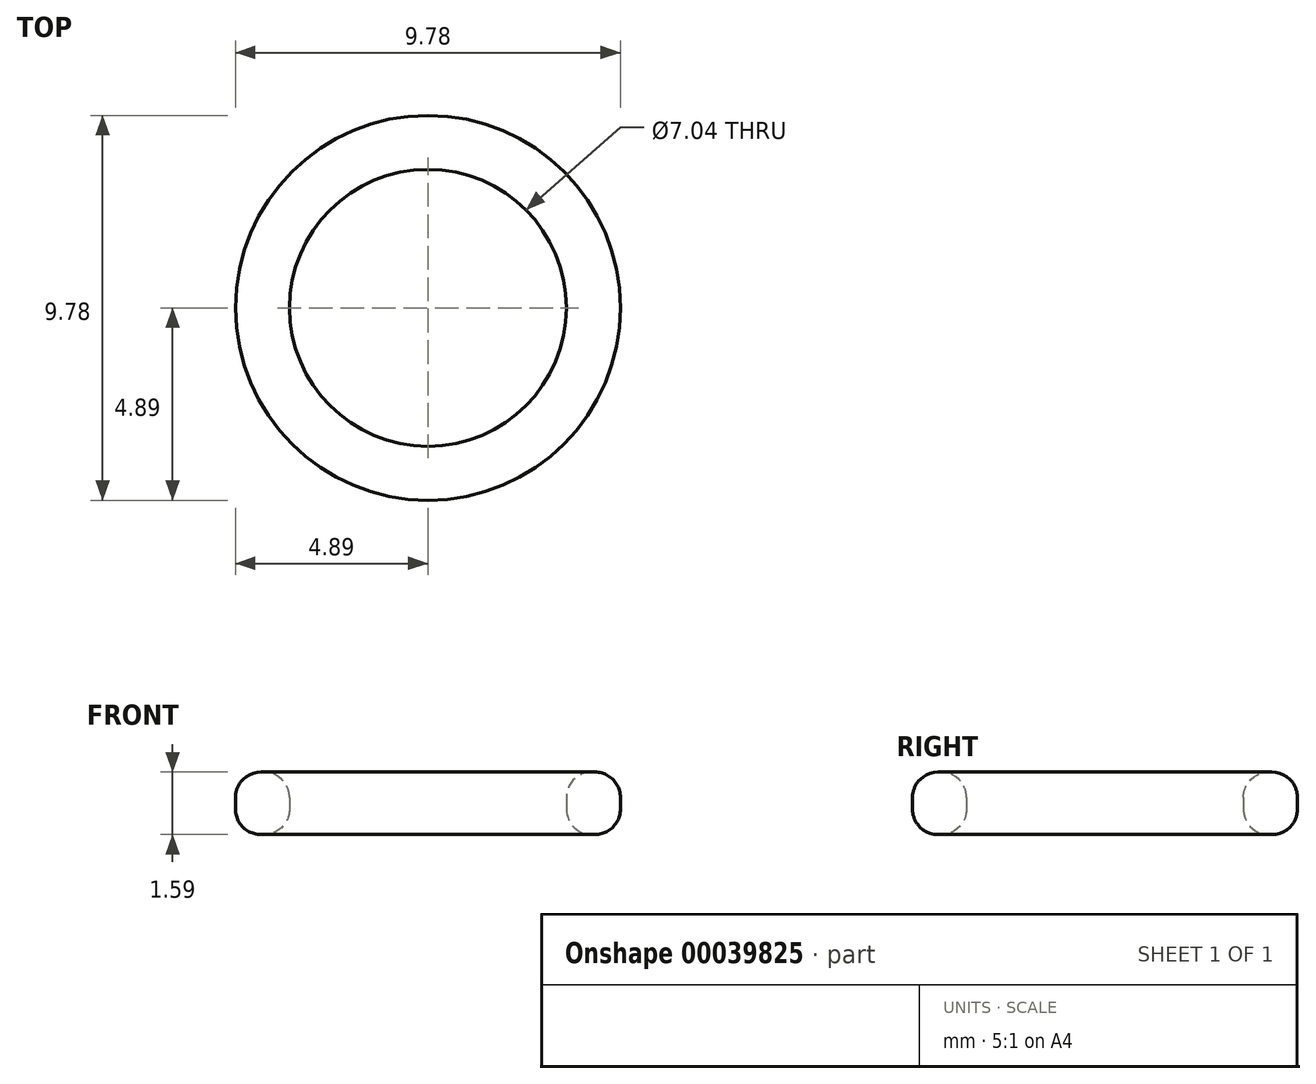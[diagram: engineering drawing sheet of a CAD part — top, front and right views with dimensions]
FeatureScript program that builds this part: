
annotation { "Feature Type Name" : "Feature", "Feature Type Description" : "" }
export const myFeature = defineFeature(function(context is Context, id is Id, definition is map)
    precondition{}
    {
        {
            var Q0;
            Q0=qCreatedBy(makeId("Top.planeOp"),FACE);
            var sketch = newSketch(context, id + "F0", { "sketchPlane" : qUnion([Q0])});
            skCircle(sketch, "E0", {"center": v(0, 0) * mm, "radius": 3.52 * mm});
            skCircle(sketch, "E1", {"center": v(0, 0) * mm, "radius": 4.89 * mm});
            skSolve(sketch);
        }
        {
            var Q0;
            Q0 = qSketchRegion(id + "F0", true);
            extrude(context, id + "F1", {"entities" : qUnion([Q0]), "depth" : 1.59 * mm});
        }
        {
            var Q0;
            Q0=makeQuery(id+"F1.opExtrude","CAP_EDGE",EDGE,{"disambiguationData":[OSD([sQuery(id+"F0.wireOp",EDGE,"E0")])],"isStart":false});
            var Q1;
            Q1=makeQuery(id+"F1.opExtrude","CAP_EDGE",EDGE,{"disambiguationData":[OSD([sQuery(id+"F0.wireOp",EDGE,"E1")])],"isStart":false});
            var Q2;
            Q2=makeQuery(id+"F1.opExtrude","CAP_EDGE",EDGE,{"disambiguationData":[OSD([sQuery(id+"F0.wireOp",EDGE,"E1")])],"isStart":true});
            var Q3;
            Q3=makeQuery(id+"F1.opExtrude","CAP_EDGE",EDGE,{"disambiguationData":[OSD([sQuery(id+"F0.wireOp",EDGE,"E0")])],"isStart":true});
            fillet(context, id + "F2", {"entities" : qUnion([Q0, Q1, Q2, Q3]), "radius" : 0.65 * mm, "tangentPropagation" : true, "allowEdgeOverflow" : false});
        }
    });
